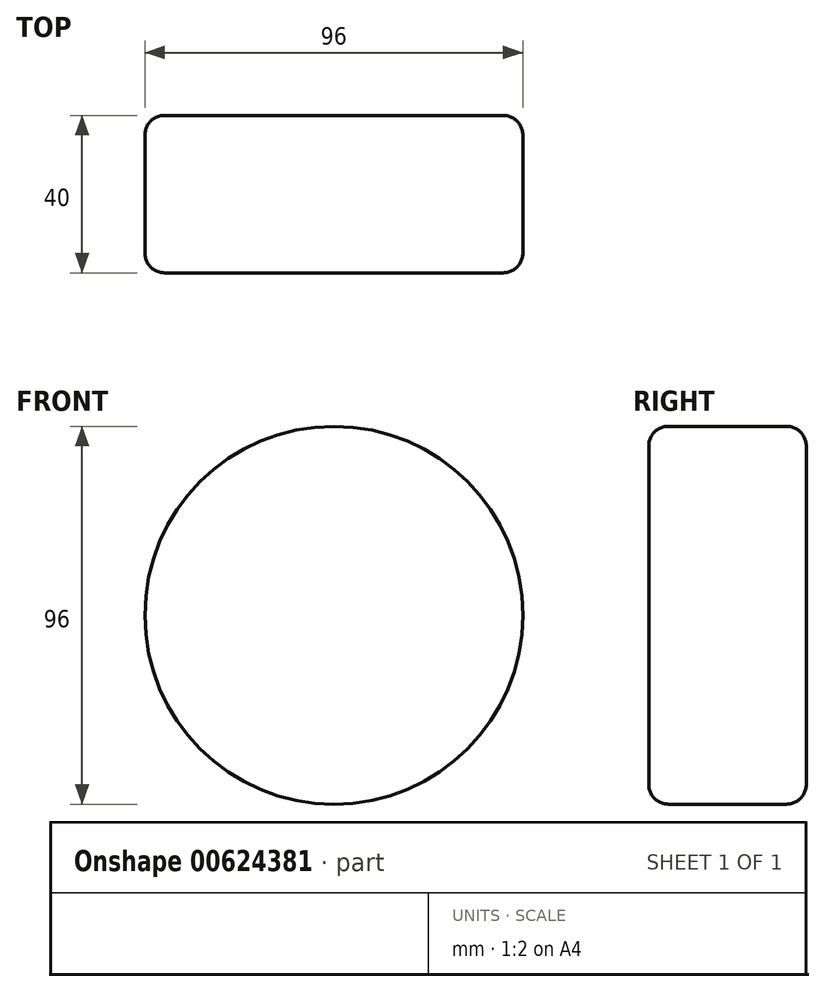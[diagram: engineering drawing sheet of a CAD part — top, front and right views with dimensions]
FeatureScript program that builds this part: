
annotation { "Feature Type Name" : "Feature", "Feature Type Description" : "" }
export const myFeature = defineFeature(function(context is Context, id is Id, definition is map)
    precondition{}
    {
        {
            var Q0;
            Q0=qCreatedBy(makeId("Front.planeOp"),FACE);
            var sketch = newSketch(context, id + "F0", { "sketchPlane" : qUnion([Q0])});
            skCircle(sketch, "E0", {"center": v(0, 0) * mm, "radius": 48 * mm});
            skSolve(sketch);
        }
        {
            var Q0;
            Q0=makeQuery(id+"F0.imprint","IMPRINT",FACE,{"disambiguationData":[TD([[makeQuery(id+"F0.imprint","IMPRINT",EDGE,{"derivedFrom":sQuery(id+"F0.wireOp",EDGE,"E0")}),1.0]])]});
            extrude(context, id + "F1", {"entities" : qUnion([Q0]), "depth" : 40 * mm, "offsetDistance" : 25 * mm});
        }
        {
            var Q0;
            Q0=makeQuery(id+"F1.opExtrude","CAP_FACE",FACE,{"disambiguationData":[OSD([sQuery(id+"F0.wireOp",EDGE,"E0")])],"isStart":false});
            fillet(context, id + "F2", {"entities" : qUnion([Q0]), "radius" : 5 * mm, "tangentPropagation" : true, "allowEdgeOverflow" : false});
        }
        {
            var Q0;
            Q0=makeQuery(id+"F1.opExtrude","SWEPT_FACE",FACE,{"disambiguationData":[OSD([sQuery(id+"F0.wireOp",EDGE,"E0")])]});
            fillet(context, id + "F3", {"entities" : qUnion([Q0]), "radius" : 5 * mm, "tangentPropagation" : true, "allowEdgeOverflow" : false});
        }
    });
